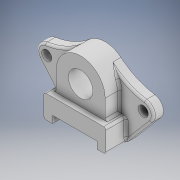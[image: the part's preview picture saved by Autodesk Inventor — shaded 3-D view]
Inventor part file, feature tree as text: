
AUTODESK INVENTOR PART (.ipt)
format: ipt  version: 2020 (Build 240168000, 168)  size: 260,608 bytes
history: native  units: mm
features: sketch x6, extrude x4, hole x2, fillet x1
ambient origin geometry x8: Origin, YZ Plane, XZ Plane, XY Plane, X Axis, Y Axis, Z Axis, Center Point
bodies: Solid1 (feature_tree)
feature tree (13):
  extrude  "Extrusion1"  Depth=95.0mm
  extrude  "Extrusion2"  Depth=67.0mm
  extrude  "Extrusion3"  Depth=50.0mm
  extrude  "Extrusion4"  Depth=14.0mm TaperAngle=0.0deg
  hole  "Hole1"  [1 undecoded]
  hole  "Hole2"  [1 undecoded]
  fillet  "Fillet1"  Radius=10.0mm
  sketch  "Sketch1"  dims[d1=28.0mm d2=95.0mm]
  sketch  "Sketch2"  dims[d3=59.0mm d4=67.0mm]
  sketch  "Sketch3"  dims[d5=86.0mm d6=50.0mm]
  sketch  "Sketch4"  dims[d7=34.0mm d8=14.0mm d9=0.0mm]
  sketch  "Sketch5"  dims[d10=32.0mm d11=28.0mm d12=0.0mm]
  sketch  "Sketch6"  dims[d13=20.0mm d14=0.0mm d15=62.0mm d16=10.0mm d17=0.0mm d18=0.0mm d19=14.0mm d20=6.0mm d21=25.4mm d22=3.048mm d23=90.0deg d24=8.0mm d25=20.594885mm d26=49.0mm d27=34.0mm d28=6.0mm d29=25.4mm d30=3.048mm d31=90.0deg d32=8.0mm d33=20.594885mm d34=3.0mm]
note: 2 required parameter values undecoded (feature->parameter linkage not recoverable at this tier; creation-order binding heuristic only, values carry confidence <= 0.55)
